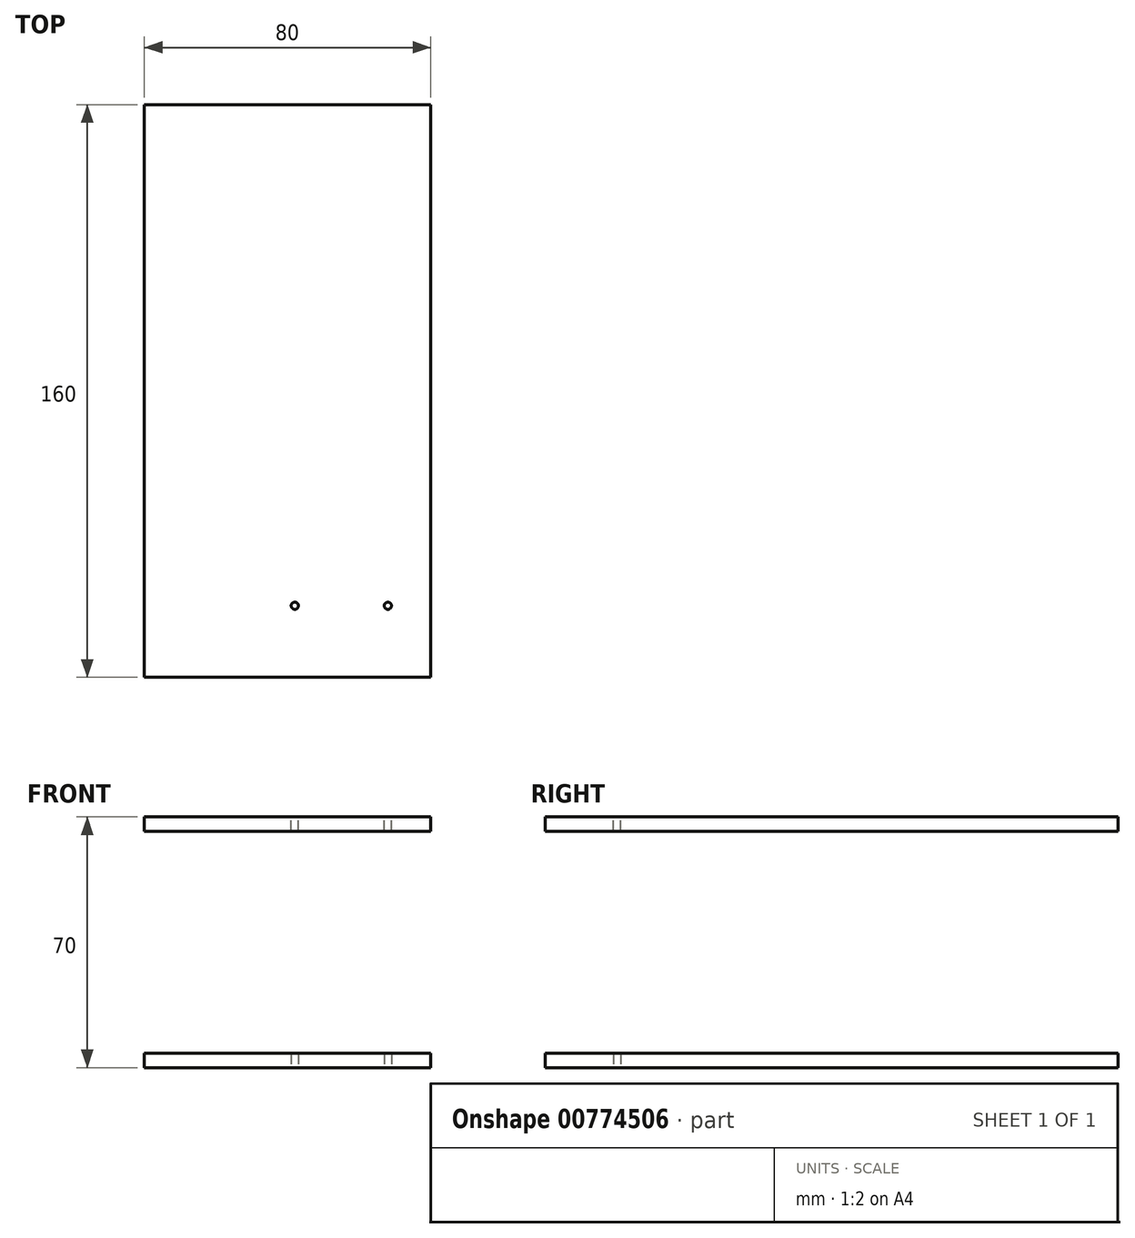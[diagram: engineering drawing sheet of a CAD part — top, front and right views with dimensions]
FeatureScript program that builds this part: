
annotation { "Feature Type Name" : "Feature", "Feature Type Description" : "" }
export const myFeature = defineFeature(function(context is Context, id is Id, definition is map)
    precondition{}
    {
        {
            var Q0;
            Q0=qCreatedBy(makeId("Top.planeOp"),FACE);
            var sketch = newSketch(context, id + "F0", { "sketchPlane" : qUnion([Q0])});
            skLineSegment(sketch, "E0.bottom", {"start": v(40, -80) * mm, "end": v(-40, -80) * mm});
            skLineSegment(sketch, "E0.top", {"start": v(40, 80) * mm, "end": v(-40, 80) * mm});
            skLineSegment(sketch, "E0.left", {"start": v(40, -80) * mm, "end": v(40, 80) * mm});
            skLineSegment(sketch, "E0.right", {"start": v(-40, -80) * mm, "end": v(-40, 80) * mm});
            skPoint(sketch, "E0.middle", {"position": v(0, 0) * mm});
            skCircle(sketch, "E1", {"center": v(2, -60) * mm, "radius": 1 * mm});
            skCircle(sketch, "E2", {"center": v(28, -60) * mm, "radius": 1 * mm});
            skSolve(sketch);
        }
        {
            var Q0;
            Q0=makeQuery(id+"F0.imprint","IMPRINT",FACE,{"disambiguationData":[TD([[makeQuery(id+"F0.imprint","IMPRINT",EDGE,{"derivedFrom":sQuery(id+"F0.wireOp",EDGE,"E0.bottom")}),-1.0]])]});
            extrude(context, id + "F1", {"entities" : qUnion([Q0]), "depth" : 4 * mm, "offsetDistance" : 25 * mm});
        }
        {
            var Q0;
            Q0=qCreatedBy(makeId("Top.planeOp"),FACE);
            cPlane(context, id + "F2", {"entities" : qUnion([Q0]), "cplaneType" : CPlaneType.OFFSET, "offset" : 35 * mm, "width" : 150 * mm, "height" : 150 * mm});
        }
        {
            var Q0;
            Q0=makeQuery(id+"F1.opExtrude","SWEPT_BODY",BODY,{"disambiguationData":[OSD([sQuery(id+"F0.wireOp",EDGE,"E0.bottom"),sQuery(id+"F0.wireOp",EDGE,"E0.top"),sQuery(id+"F0.wireOp",EDGE,"E0.left"),sQuery(id+"F0.wireOp",EDGE,"E0.right")])]});
            var Q1;
            Q1=qCreatedBy(id+"F2.planeOp",FACE);
            mirror(context, id + "F3", {"entities" : qUnion([Q0]), "mirrorPlane" : qUnion([Q1])});
        }
    });
